# Revit family: Секция смешения двухэтажная AIRNED-M S2
name_source: partatom
category: Оборудование
revit_build: Autodesk Revit 2017 (Build: 20160225_1515(x64)
units: mm (PartAtom-declared; Revit-internal decimal feet)

## family parameters
Всегда вертикально = Да
На основе рабочей плоскости = Нет
Общий = Нет
При загрузке вырезать с полостями = Нет
Размер круглого соединителя = Использовать диаметр
Тип детали = Нормальный
Точка расчета площади = Нет

## types (6) — shared parameters
h = 130 мм
Единица измерения = шт.
Завод изготовитель = NED
Ключевая пометка = Вентиляция
Материал = Сталь серая
Наименование и тех.хар-ка = Секция смешения двухэтажная
Раздел = ОВ
высота ножек = 120 мм

## per-type parameters (varying)
| type | А | А1 | Б | Б1 | Высота | Д | Д1 | Середина | Ширина | центр |
| AIRNED-M 6 S2 | 1100 мм | 1080 мм | 2153 мм | 1057 мм | 1001 мм | 575 мм | 555 мм | 1077 мм | 1024 мм | 538 мм |
| AIRNED-M 7 S2 | 1100 мм | 1080 мм | 2593 мм | 1277 мм | 1221 мм | 575 мм | 555 мм | 1297 мм | 1024 мм | 648 мм |
| AIRNED-M 8 S2 | 1320 мм | 1300 мм | 2593 мм | 1277 мм | 1221 мм | 575 мм | 555 мм | 1297 мм | 1244 мм | 648 мм |
| AIRNED-M 12 S2 | 1435 мм | 1415 мм | 2823 мм | 1392 мм | 1336 мм | 1100 мм | 1080 мм | 1412 мм | 1359 мм | 706 мм |
| AIRNED-M 20 S2 | 1660 мм | 1640 мм | 3273 мм | 1617 мм | 1561 мм | 1100 мм | 1080 мм | 1637 мм | 1584 мм | 818 мм |
| AIRNED-M 25 S2 | 2045 мм | 2025 мм | 4043 мм | 2002 мм | 1946 мм | 1100 мм | 1080 мм | 2022 мм | 1969 мм | 1011 мм |

note: column(s) folded — value = type name in every type: Тип, марка, обозначение
